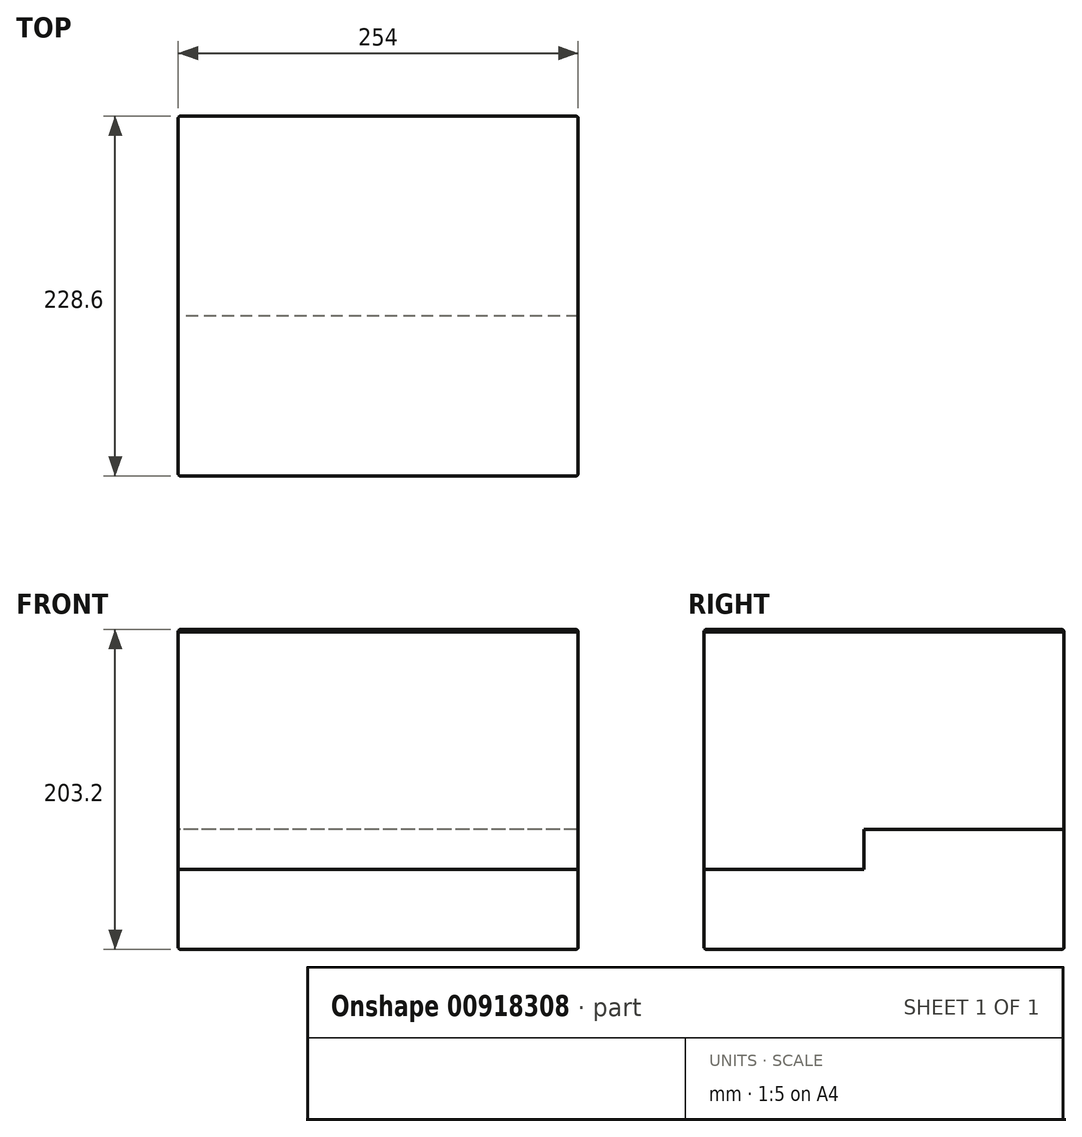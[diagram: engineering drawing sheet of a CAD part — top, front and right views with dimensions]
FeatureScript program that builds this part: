
annotation { "Feature Type Name" : "Feature", "Feature Type Description" : "" }
export const myFeature = defineFeature(function(context is Context, id is Id, definition is map)
    precondition{}
    {
        {
            var Q0;
            Q0=qCreatedBy(makeId("Front.planeOp"),FACE);
            var sketch = newSketch(context, id + "F0", { "sketchPlane" : qUnion([Q0])});
            skLineSegment(sketch, "E0.bottom", {"start": v(127, 114.3) * mm, "end": v(-127, 114.3) * mm});
            skLineSegment(sketch, "E0.top", {"start": v(127, -114.3) * mm, "end": v(-127, -114.3) * mm});
            skLineSegment(sketch, "E0.left", {"start": v(127, 114.3) * mm, "end": v(127, -114.3) * mm});
            skLineSegment(sketch, "E0.right", {"start": v(-127, 114.3) * mm, "end": v(-127, -114.3) * mm});
            skPoint(sketch, "E0.middle", {"position": v(0, 0) * mm});
            skLineSegment(sketch, "E1", {"start": v(-127, 0) * mm, "end": v(127, 0) * mm, "construction": true});
            skSolve(sketch);
        }
        {
            var Q0;
            Q0=makeQuery(id+"F0.imprint","IMPRINT",FACE,{"disambiguationData":[TD([[makeQuery(id+"F0.imprint","IMPRINT",EDGE,{"derivedFrom":sQuery(id+"F0.wireOp",EDGE,"E0.bottom")}),1.0]])]});
            extrude(context, id + "F1", {"entities" : qUnion([Q0]), "endBound" : BoundingType.SYMMETRIC, "depth" : 203.2 * mm, "offsetDistance" : 25.4 * mm});
        }
        {
            var Q0;
            Q0=makeQuery(id+"F1.opExtrude","CAP_FACE",FACE,{"disambiguationData":[OSD([sQuery(id+"F0.wireOp",EDGE,"E0.bottom"),sQuery(id+"F0.wireOp",EDGE,"E0.top"),sQuery(id+"F0.wireOp",EDGE,"E0.left"),sQuery(id+"F0.wireOp",EDGE,"E0.right")])],"isStart":false});
            var Q1;
            Q1=makeQuery(id+"F1.opExtrude","CAP_FACE",FACE,{"disambiguationData":[OSD([sQuery(id+"F0.wireOp",EDGE,"E0.bottom"),sQuery(id+"F0.wireOp",EDGE,"E0.top"),sQuery(id+"F0.wireOp",EDGE,"E0.left"),sQuery(id+"F0.wireOp",EDGE,"E0.right")])],"isStart":true});
            var Q2;
            Q2=makeQuery(id+"F1.opExtrude","SWEPT_FACE",FACE,{"disambiguationData":[OSD([sQuery(id+"F0.wireOp",EDGE,"E0.bottom")])]});
            var Q3;
            Q3=makeQuery(id+"F1.opExtrude","SWEPT_FACE",FACE,{"disambiguationData":[OSD([sQuery(id+"F0.wireOp",EDGE,"E0.top")])]});
            fillet(context, id + "F2", {"entities" : qUnion([Q0, Q1, Q2, Q3]), "radius" : 1.52 * mm, "tangentPropagation" : true, "allowEdgeOverflow" : false});
        }
        {
            var Q0;
            Q0=qCreatedBy(makeId("Right.planeOp"),FACE);
            var sketch = newSketch(context, id + "F3", { "sketchPlane" : qUnion([Q0])});
            skLineSegment(sketch, "E2", {"start": v(-100.08, 114.3) * mm, "end": v(-100.08, -114.3) * mm});
            skLineSegment(sketch, "E3", {"start": v(-100.08, -114.3) * mm, "end": v(50.8, -114.3) * mm});
            skLineSegment(sketch, "E4", {"start": v(50.8, -114.3) * mm, "end": v(50.8, -12.7) * mm});
            skLineSegment(sketch, "E5", {"start": v(50.8, -12.7) * mm, "end": v(25.4, -12.7) * mm});
            skLineSegment(sketch, "E6", {"start": v(25.4, -12.7) * mm, "end": v(25.4, 114.3) * mm});
            skLineSegment(sketch, "E7", {"start": v(25.4, 114.3) * mm, "end": v(-100.08, 114.3) * mm});
            skSolve(sketch);
        }
        {
            var Q0;
            Q0=qSketchRegion(id+"F3",true);
            extrude(context, id + "F4", {"entities" : qUnion([Q0]), "endBound" : BoundingType.SYMMETRIC, "depth" : 254 * mm, "offsetDistance" : 25.4 * mm});
        }
        {
            var Q0;
            Q0=makeQuery(id+"F4.opExtrude","SWEPT_BODY",BODY,{"disambiguationData":[OSD([sQuery(id+"F3.wireOp",EDGE,"E2"),sQuery(id+"F3.wireOp",EDGE,"E3"),sQuery(id+"F3.wireOp",EDGE,"E4"),sQuery(id+"F3.wireOp",EDGE,"E5"),sQuery(id+"F3.wireOp",EDGE,"E6"),sQuery(id+"F3.wireOp",EDGE,"E7")])]});
            var Q1;
            Q1=makeQuery(id+"F1.opExtrude","SWEPT_BODY",BODY,{"disambiguationData":[OSD([sQuery(id+"F0.wireOp",EDGE,"E0.bottom"),sQuery(id+"F0.wireOp",EDGE,"E0.top"),sQuery(id+"F0.wireOp",EDGE,"E0.left"),sQuery(id+"F0.wireOp",EDGE,"E0.right")])]});
            booleanBodies(context, id + "F5", {"operationType" : BooleanOperationType.SUBTRACTION, "tools" : qUnion([Q0]), "targets" : qUnion([Q1]), "keepTools" : true});
        }
        {
            var Q0;
            Q0=makeQuery(id+"F4.opExtrude","CAP_EDGE",EDGE,{"disambiguationData":[OSD([sQuery(id+"F3.wireOp",EDGE,"E7")])],"isStart":false});
            var Q1;
            Q1=makeQuery(id+"F4.opExtrude","CAP_EDGE",EDGE,{"disambiguationData":[OSD([sQuery(id+"F3.wireOp",EDGE,"E3")])],"isStart":false});
            var Q2;
            Q2=makeQuery(id+"F4.opExtrude","CAP_EDGE",EDGE,{"disambiguationData":[OSD([sQuery(id+"F3.wireOp",EDGE,"E3")])],"isStart":true});
            var Q3;
            Q3=makeQuery(id+"F4.opExtrude","CAP_EDGE",EDGE,{"disambiguationData":[OSD([sQuery(id+"F3.wireOp",EDGE,"E7")])],"isStart":true});
            fillet(context, id + "F6", {"entities" : qUnion([Q0, Q1, Q2, Q3]), "radius" : 1.52 * mm, "tangentPropagation" : true, "allowEdgeOverflow" : false});
        }
        {
            var Q0;
            Q0=makeQuery(id+"F5.opBoolean","SPLIT",BODY,{"disambiguationData":[OD(1.0)],"derivedFrom":makeQuery(id+"F1.opExtrude","SWEPT_BODY",BODY,{"disambiguationData":[OSD([sQuery(id+"F0.wireOp",EDGE,"E0.bottom"),sQuery(id+"F0.wireOp",EDGE,"E0.top"),sQuery(id+"F0.wireOp",EDGE,"E0.left"),sQuery(id+"F0.wireOp",EDGE,"E0.right")])]})});
            var Q1;
            Q1=makeQuery(id+"F4.opExtrude","SWEPT_BODY",BODY,{"disambiguationData":[OSD([sQuery(id+"F3.wireOp",EDGE,"E2"),sQuery(id+"F3.wireOp",EDGE,"E3"),sQuery(id+"F3.wireOp",EDGE,"E4"),sQuery(id+"F3.wireOp",EDGE,"E5"),sQuery(id+"F3.wireOp",EDGE,"E6"),sQuery(id+"F3.wireOp",EDGE,"E7")])]});
            var Q2;
            Q2=makeQuery(id+"F5.opBoolean","SPLIT",BODY,{"disambiguationData":[OD(0.0)],"derivedFrom":makeQuery(id+"F1.opExtrude","SWEPT_BODY",BODY,{"disambiguationData":[OSD([sQuery(id+"F0.wireOp",EDGE,"E0.bottom"),sQuery(id+"F0.wireOp",EDGE,"E0.top"),sQuery(id+"F0.wireOp",EDGE,"E0.left"),sQuery(id+"F0.wireOp",EDGE,"E0.right")])]})});
            var Q3;
            Q3=sQuery(id+"F0.wireOp",EDGE,"E1");
            transform(context, id + "F7", {"entities" : qUnion([Q0, Q1, Q2]), "transformType" : TransformType.ROTATION, "transformAxis" : qUnion([Q3]), "angle" : 90 * degree, "oppositeDirection" : true, "makeCopy" : false});
        }
    });
